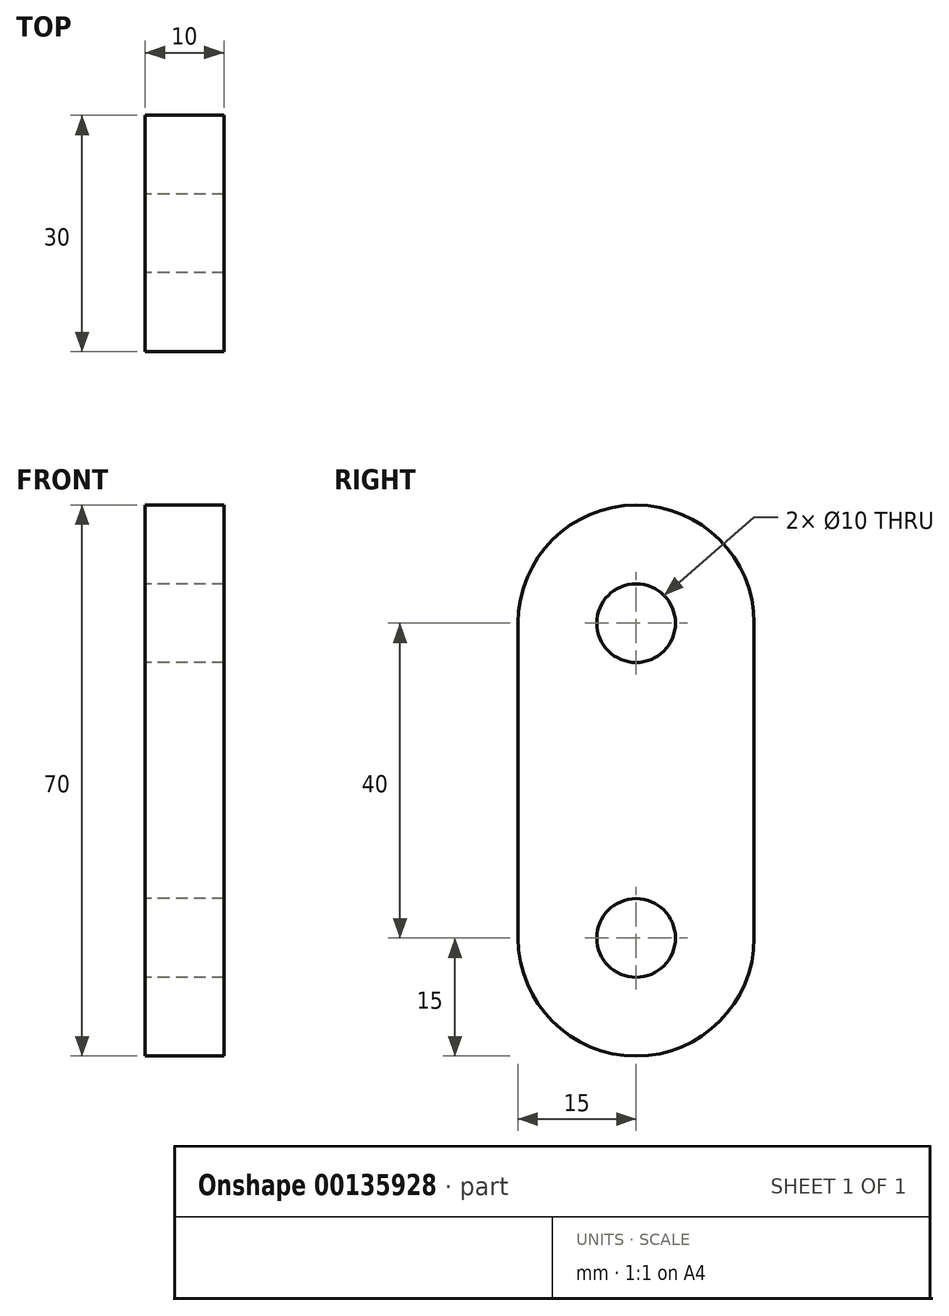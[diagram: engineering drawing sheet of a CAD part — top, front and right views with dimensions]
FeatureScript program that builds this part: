
annotation { "Feature Type Name" : "Feature", "Feature Type Description" : "" }
export const myFeature = defineFeature(function(context is Context, id is Id, definition is map)
    precondition{}
    {
        {
            var Q0;
            Q0=qCreatedBy(makeId("Right.planeOp"),FACE);
            var sketch = newSketch(context, id + "F0", { "sketchPlane" : qUnion([Q0])});
            skCircle(sketch, "E0", {"center": v(0, 0) * mm, "radius": 5 * mm});
            skArc(sketch, "E1", {"start": v(-15, 0) * mm, "mid": v(0, -15) * mm, "end": v(15, 0) * mm});
            skLineSegment(sketch, "E2", {"start": v(0, 0) * mm, "end": v(5, 0) * mm});
            skLineSegment(sketch, "E3", {"start": v(-15, 0) * mm, "end": v(-15, 40) * mm});
            skLineSegment(sketch, "E4", {"start": v(15, 0) * mm, "end": v(15, 40) * mm});
            skCircle(sketch, "E5", {"center": v(0, 40) * mm, "radius": 5 * mm});
            skArc(sketch, "E6", {"start": v(15, 40) * mm, "mid": v(0, 55) * mm, "end": v(-15, 40) * mm});
            skLineSegment(sketch, "E7", {"start": v(0, 0) * mm, "end": v(15, 0) * mm});
            skLineSegment(sketch, "E8", {"start": v(0, 40) * mm, "end": v(15, 40) * mm});
            skLineSegment(sketch, "E9", {"start": v(-15, 40) * mm, "end": v(15, 40) * mm});
            skSolve(sketch);
        }
        {
            var Q0;
            Q0=qSketchRegion(id+"F0",true);
            extrude(context, id + "F1", {"entities" : qUnion([Q0]), "depth" : 10 * mm});
        }
    });
